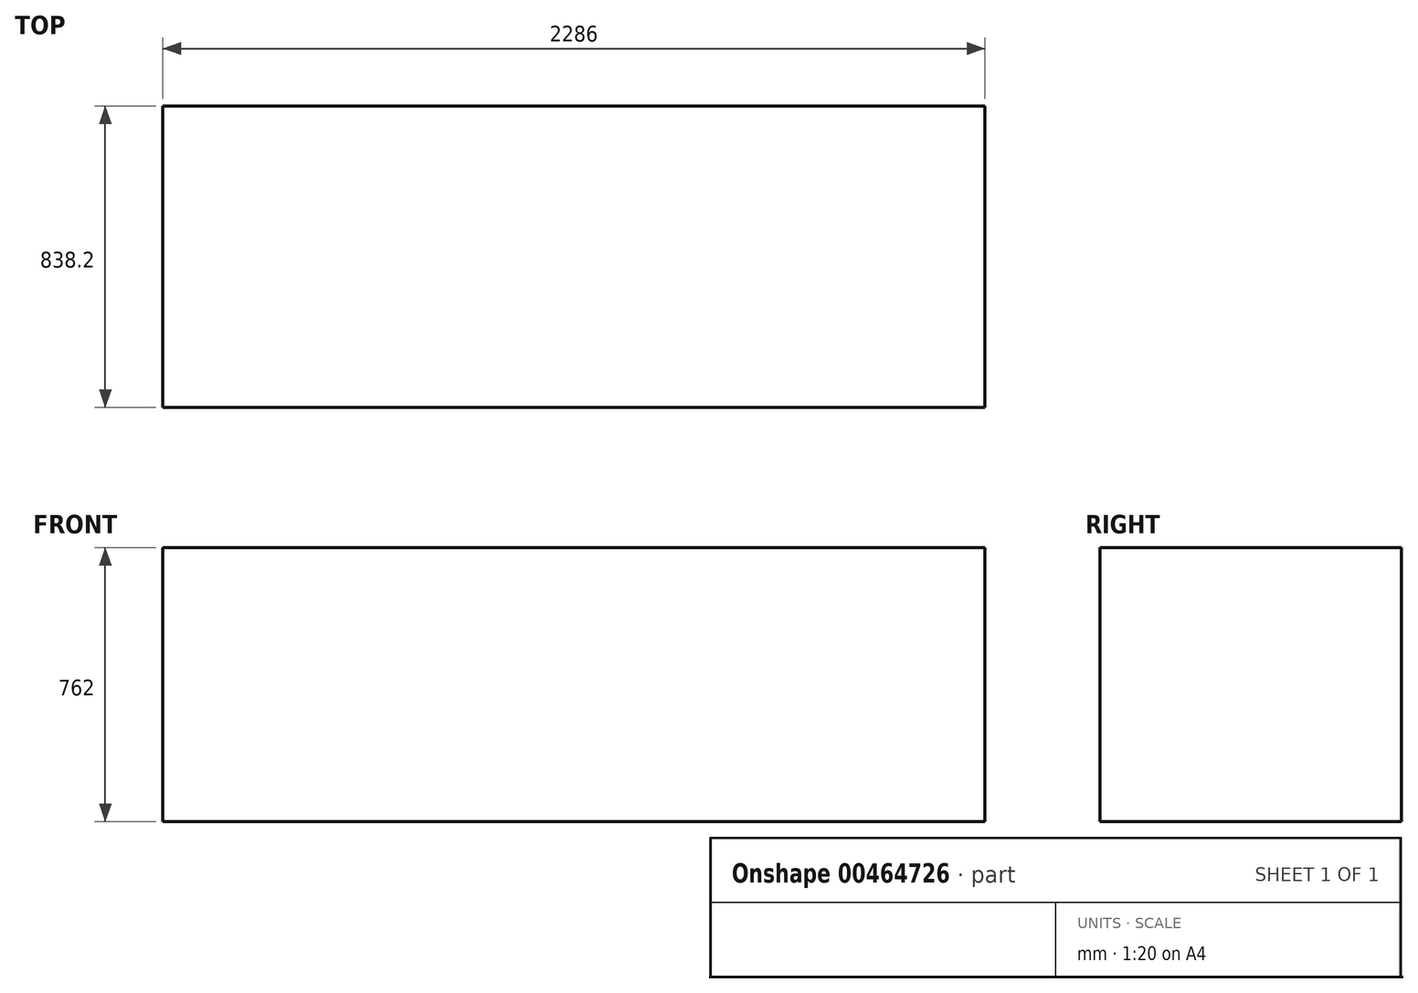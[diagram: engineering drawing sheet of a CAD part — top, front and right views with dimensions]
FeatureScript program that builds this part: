
annotation { "Feature Type Name" : "Feature", "Feature Type Description" : "" }
export const myFeature = defineFeature(function(context is Context, id is Id, definition is map)
    precondition{}
    {
        {
            var Q0;
            Q0=qCreatedBy(makeId("Top.planeOp"),FACE);
            var sketch = newSketch(context, id + "F0", { "sketchPlane" : qUnion([Q0])});
            skLineSegment(sketch, "E0.bottom", {"start": v(1143, -419.1) * mm, "end": v(-1143, -419.1) * mm});
            skLineSegment(sketch, "E0.top", {"start": v(1143, 419.1) * mm, "end": v(-1143, 419.1) * mm});
            skLineSegment(sketch, "E0.left", {"start": v(1143, -419.1) * mm, "end": v(1143, 419.1) * mm});
            skLineSegment(sketch, "E0.right", {"start": v(-1143, -419.1) * mm, "end": v(-1143, 419.1) * mm});
            skPoint(sketch, "E0.middle", {"position": v(0, 0) * mm});
            skSolve(sketch);
        }
        {
            var Q0;
            Q0=makeQuery(id+"F0.imprint","IMPRINT",FACE,{"disambiguationData":[TD([[makeQuery(id+"F0.imprint","IMPRINT",EDGE,{"derivedFrom":sQuery(id+"F0.wireOp",EDGE,"E0.bottom")}),-1.0]])]});
            extrude(context, id + "F1", {"entities" : qUnion([Q0]), "depth" : 762 * mm});
        }
    });
